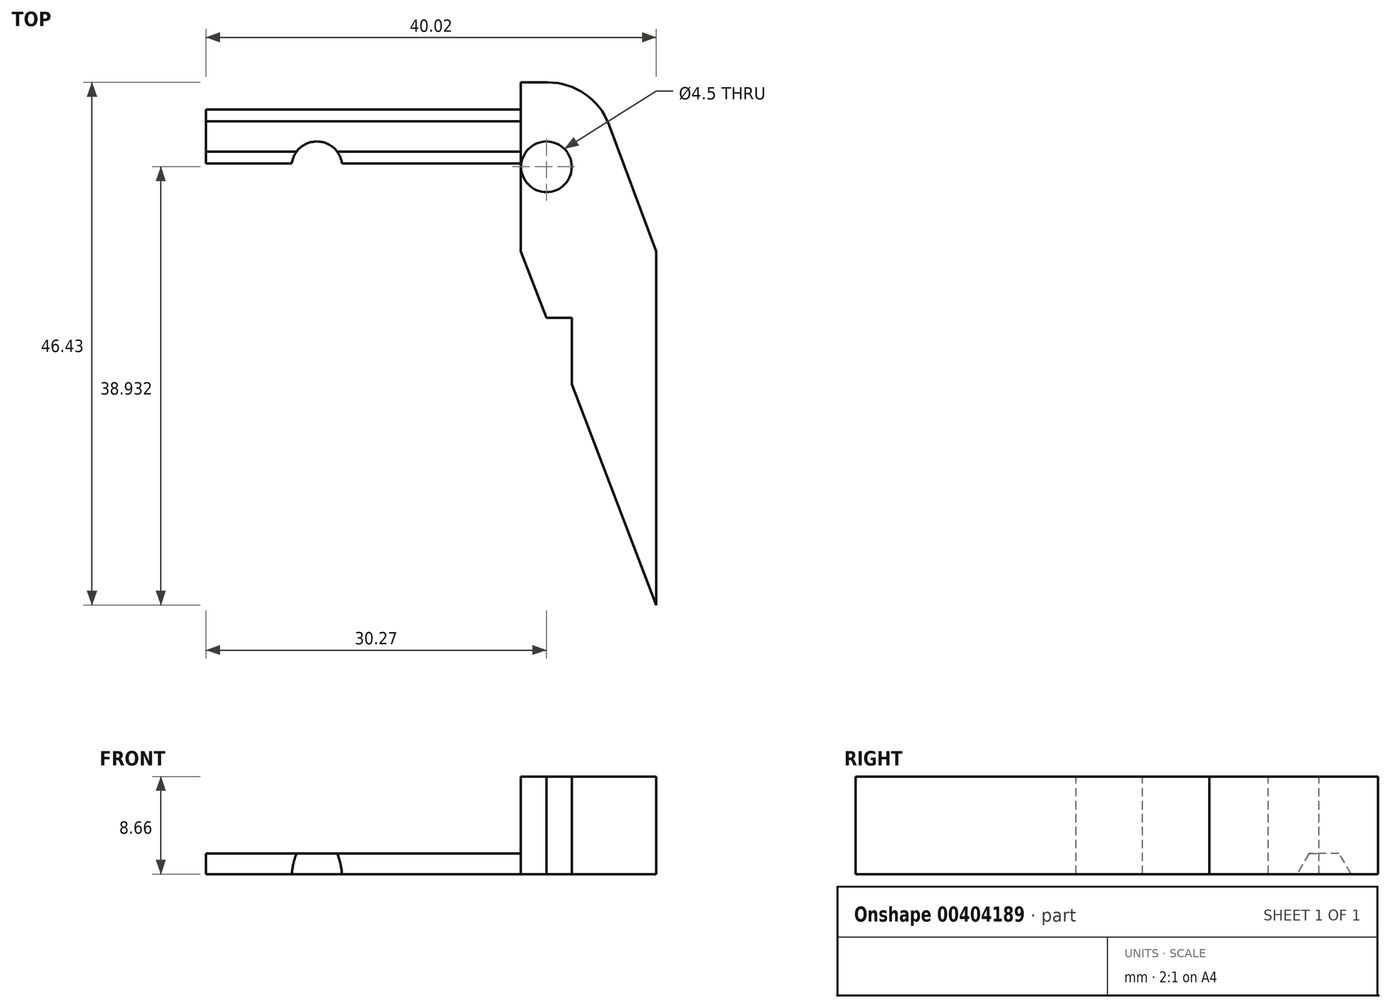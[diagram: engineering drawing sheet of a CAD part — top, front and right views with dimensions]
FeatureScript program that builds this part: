
annotation { "Feature Type Name" : "Feature", "Feature Type Description" : "" }
export const myFeature = defineFeature(function(context is Context, id is Id, definition is map)
    precondition{}
    {
        {
            var Q0;
            Q0=qCreatedBy(makeId("Top.planeOp"),FACE);
            var sketch = newSketch(context, id + "F0", { "sketchPlane" : qUnion([Q0])});
            skLineSegment(sketch, "E0", {"start": v(0, 27.49) * mm, "end": v(0, 58.92) * mm});
            skLineSegment(sketch, "E1", {"start": v(0, 58.92) * mm, "end": v(-12.02, 58.92) * mm, "construction": true});
            skLineSegment(sketch, "E2", {"start": v(-9.76, 53) * mm, "end": v(-7.5, 53) * mm});
            skLineSegment(sketch, "E3", {"start": v(-7.5, 53) * mm, "end": v(-7.5, 47.1) * mm});
            skLineSegment(sketch, "E4", {"start": v(-7.5, 47.1) * mm, "end": v(0, 27.49) * mm});
            skLineSegment(sketch, "E5", {"start": v(-12.02, 58.92) * mm, "end": v(-12.02, 73.92) * mm});
            skLineSegment(sketch, "E6", {"start": v(-12.02, 77.72) * mm, "end": v(-7.02, 77.72) * mm, "construction": true});
            skLineSegment(sketch, "E7", {"start": v(-5.6, 73.92) * mm, "end": v(0, 58.92) * mm});
            skCircle(sketch, "E8", {"center": v(-9.75, 66.42) * mm, "radius": 2.25 * mm});
            skLineSegment(sketch, "E9", {"start": v(-12.02, 73.92) * mm, "end": v(-5.6, 73.92) * mm});
            skLineSegment(sketch, "E10", {"start": v(-9.76, 53) * mm, "end": v(-12.02, 58.92) * mm});
            skSolve(sketch);
        }
        {
            var Q0;
            Q0=qSketchRegion(id+"F0",true);
            extrude(context, id + "F1", {"entities" : qUnion([Q0]), "endBound" : BoundingType.SYMMETRIC, "oppositeDirection" : true, "depth" : 8.66 * mm});
        }
        {
            var Q0;
            Q0=makeQuery(id+"F1.opExtrude","SWEPT_EDGE",EDGE,{"disambiguationData":[OSD([sQuery(id+"F0.wireOp",EDGE,"E7"),sQuery(id+"F0.wireOp",EDGE,"E9")])]});
            fillet(context, id + "F2", {"entities" : qUnion([Q0]), "radius" : 5.8 * mm, "tangentPropagation" : true, "allowEdgeOverflow" : false});
        }
        {
            var Q0;
            Q0=makeQuery(id+"F1.opExtrude","SWEPT_FACE",FACE,{"disambiguationData":[OSD([sQuery(id+"F0.wireOp",EDGE,"E5")])]});
            var sketch = newSketch(context, id + "F3", { "sketchPlane" : qUnion([Q0])});
            skCircle(sketch, "E11.cCircle", {"center": v(-69.12, -4.33) * mm, "radius": 2.08 * mm, "construction": true});
            skLineSegment(sketch, "E11.0", {"start": v(-67.92, -6.4) * mm, "end": v(-70.32, -6.4) * mm, "construction": true});
            skLineSegment(sketch, "E11.1", {"start": v(-70.32, -6.4) * mm, "end": v(-71.52, -4.33) * mm, "construction": true});
            skLineSegment(sketch, "E11.2", {"start": v(-71.52, -4.33) * mm, "end": v(-70.47, -2.5) * mm});
            skLineSegment(sketch, "E11.3", {"start": v(-70.32, -2.25) * mm, "end": v(-67.92, -2.25) * mm, "construction": true});
            skLineSegment(sketch, "E11.4", {"start": v(-67.78, -2.5) * mm, "end": v(-66.72, -4.33) * mm});
            skLineSegment(sketch, "E11.5", {"start": v(-66.72, -4.33) * mm, "end": v(-67.92, -6.4) * mm, "construction": true});
            skPoint(sketch, "E11.0.midPoint", {"position": v(-69.12, -6.4) * mm});
            skLineSegment(sketch, "E12", {"start": v(-71.52, -4.33) * mm, "end": v(-66.72, -4.33) * mm});
            skLineSegment(sketch, "E13", {"start": v(-70.47, -2.5) * mm, "end": v(-67.78, -2.5) * mm});
            skSolve(sketch);
        }
        {
            var Q0;
            Q0 = qSketchRegion(id + "F3", true);
            var Q1;
            Q1=sQuery(id+"F3.wireOp",EDGE,"38b882f9-1936-4e65-8a5b-acd813efc6e7.3");
            var Q2;
            Q2=sQuery(id+"F3.wireOp",EDGE,"8802f2cc-5fe1-4b28-b249-121c3e666989.3");
            extrude(context, id + "F4", {"entities" : qUnion([Q0]), "operationType" : NewBodyOperationType.ADD, "surfaceEntities" : qUnion([Q1, Q2]), "depth" : 28 * mm});
        }
        {
            var Q0;
            Q0=makeQuery(id+"F1.opExtrude","CAP_FACE",FACE,{"disambiguationData":[OSD([sQuery(id+"F0.wireOp",EDGE,"E0"),sQuery(id+"F0.wireOp",EDGE,"E2"),sQuery(id+"F0.wireOp",EDGE,"E3"),sQuery(id+"F0.wireOp",EDGE,"E4"),sQuery(id+"F0.wireOp",EDGE,"E5"),sQuery(id+"F0.wireOp",EDGE,"E7"),sQuery(id+"F0.wireOp",EDGE,"E8"),sQuery(id+"F0.wireOp",EDGE,"E9"),sQuery(id+"F0.wireOp",EDGE,"E10")])],"isStart":true});
            var sketch = newSketch(context, id + "F5", { "sketchPlane" : qUnion([Q0])});
            skCircle(sketch, "E14", {"center": v(-30.15, 66.42) * mm, "radius": 2.25 * mm});
            skCircle(sketch, "E15", {"center": v(-9.75, 66.42) * mm, "radius": 2.25 * mm, "construction": true});
            skSolve(sketch);
        }
        {
            var Q0;
            Q0 = qSketchRegion(id + "F5", true);
            extrude(context, id + "F6", {"entities" : qUnion([Q0]), "operationType" : NewBodyOperationType.REMOVE, "oppositeDirection" : true, "depth" : 25 * mm});
        }
    });
